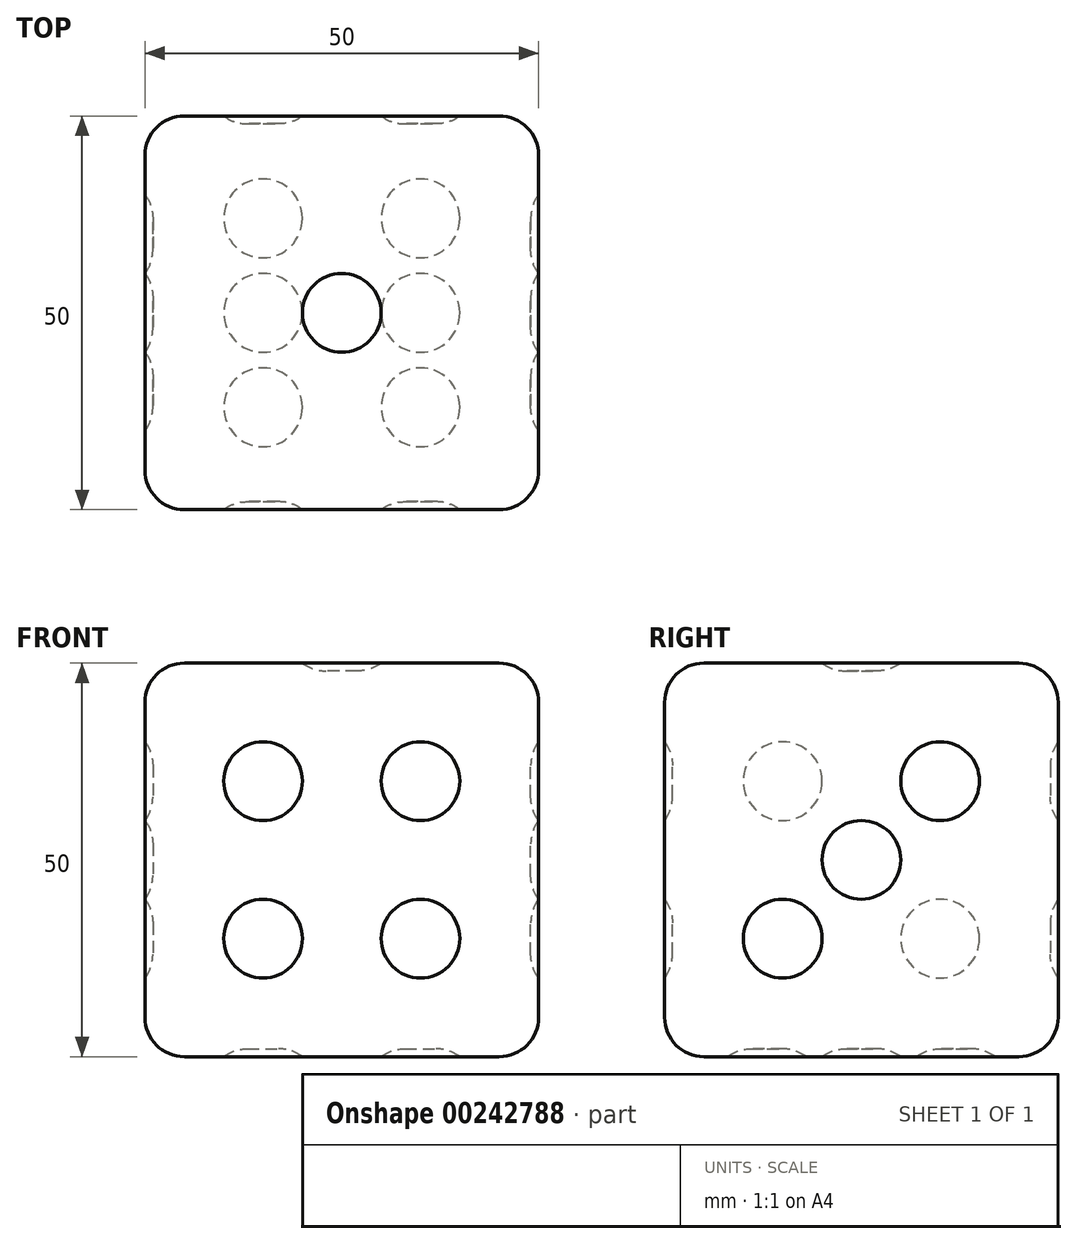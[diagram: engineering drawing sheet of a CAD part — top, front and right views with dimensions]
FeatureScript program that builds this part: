
annotation { "Feature Type Name" : "Feature", "Feature Type Description" : "" }
export const myFeature = defineFeature(function(context is Context, id is Id, definition is map)
    precondition{}
    {
        {
            var Q0;
            Q0=qCreatedBy(makeId("Top.planeOp"),FACE);
            var sketch = newSketch(context, id + "F0", { "sketchPlane" : qUnion([Q0])});
            skLineSegment(sketch, "E0", {"start": v(50, 0) * mm, "end": v(50, -50) * mm});
            skLineSegment(sketch, "E1", {"start": v(0, 0) * mm, "end": v(0, -50) * mm});
            skLineSegment(sketch, "E2", {"start": v(50, -50) * mm, "end": v(0, -50) * mm});
            skLineSegment(sketch, "E3", {"start": v(50, 0) * mm, "end": v(0, 0) * mm});
            skSolve(sketch);
        }
        {
            var Q0;
            Q0=makeQuery(id+"F0.imprint","IMPRINT",FACE,{"disambiguationData":[TD([[makeQuery(id+"F0.imprint","IMPRINT",EDGE,{"derivedFrom":sQuery(id+"F0.wireOp",EDGE,"E0")}),-1.0]])]});
            extrude(context, id + "F1", {"entities" : qUnion([Q0]), "depth" : 50 * mm});
        }
        {
            var Q0;
            Q0=makeQuery(id+"F1.opExtrude","CAP_FACE",FACE,{"disambiguationData":[OSD([sQuery(id+"F0.wireOp",EDGE,"E0"),sQuery(id+"F0.wireOp",EDGE,"E1"),sQuery(id+"F0.wireOp",EDGE,"E2"),sQuery(id+"F0.wireOp",EDGE,"E3")])],"isStart":false});
            var sketch = newSketch(context, id + "F2", { "sketchPlane" : qUnion([Q0])});
            skCircle(sketch, "E4", {"center": v(25, -25) * mm, "radius": 5 * mm});
            skSolve(sketch);
        }
        {
            var Q0;
            Q0=makeQuery(id+"F2.imprint","IMPRINT",FACE,{"disambiguationData":[TD([[makeQuery(id+"F2.imprint","IMPRINT",EDGE,{"derivedFrom":sQuery(id+"F2.wireOp",EDGE,"E4")}),1.0]])]});
            extrude(context, id + "F3", {"entities" : qUnion([Q0]), "operationType" : NewBodyOperationType.REMOVE, "oppositeDirection" : true, "depth" : 1 * mm});
        }
        {
            var Q0;
            Q0=makeQuery(id+"F1.opExtrude","SWEPT_EDGE",EDGE,{"disambiguationData":[OSD([sQuery(id+"F0.wireOp",EDGE,"E1"),sQuery(id+"F0.wireOp",EDGE,"E2")])]});
            var Q1;
            Q1=makeQuery(id+"F1.opExtrude","CAP_EDGE",EDGE,{"disambiguationData":[OSD([sQuery(id+"F0.wireOp",EDGE,"E2")])],"isStart":false});
            var Q2;
            Q2=makeQuery(id+"F1.opExtrude","CAP_EDGE",EDGE,{"disambiguationData":[OSD([sQuery(id+"F0.wireOp",EDGE,"E3")])],"isStart":false});
            var Q3;
            Q3=makeQuery(id+"F1.opExtrude","SWEPT_FACE",FACE,{"disambiguationData":[OSD([sQuery(id+"F0.wireOp",EDGE,"E1")])]});
            var Q4;
            Q4=makeQuery(id+"F1.opExtrude","CAP_EDGE",EDGE,{"disambiguationData":[OSD([sQuery(id+"F0.wireOp",EDGE,"E2")])],"isStart":true});
            var Q5;
            Q5=makeQuery(id+"F1.opExtrude","SWEPT_EDGE",EDGE,{"disambiguationData":[OSD([sQuery(id+"F0.wireOp",EDGE,"E0"),sQuery(id+"F0.wireOp",EDGE,"E2")])]});
            var Q6;
            Q6=makeQuery(id+"F1.opExtrude","CAP_EDGE",EDGE,{"disambiguationData":[OSD([sQuery(id+"F0.wireOp",EDGE,"E3")])],"isStart":true});
            var Q7;
            Q7=makeQuery(id+"F1.opExtrude","SWEPT_EDGE",EDGE,{"disambiguationData":[OSD([sQuery(id+"F0.wireOp",EDGE,"E0"),sQuery(id+"F0.wireOp",EDGE,"E3")])]});
            var Q8;
            Q8=makeQuery(id+"F1.opExtrude","CAP_EDGE",EDGE,{"disambiguationData":[OSD([sQuery(id+"F0.wireOp",EDGE,"E0")])],"isStart":true});
            var Q9;
            Q9=makeQuery(id+"F1.opExtrude","CAP_EDGE",EDGE,{"disambiguationData":[OSD([sQuery(id+"F0.wireOp",EDGE,"E0")])],"isStart":false});
            fillet(context, id + "F4", {"entities" : qUnion([Q0, Q1, Q2, Q3, Q4, Q5, Q6, Q7, Q8, Q9]), "radius" : 5 * mm, "tangentPropagation" : true, "allowEdgeOverflow" : false});
        }
        {
            var Q0;
            Q0=makeQuery(id+"F3.opExtrude","CAP_EDGE",EDGE,{"disambiguationData":[OSD([sQuery(id+"F2.wireOp",EDGE,"E4")])],"isStart":false});
            var Q1;
            Q1=makeQuery(id+"F3.boolean.opBoolean","COPY",EDGE,{"derivedFrom":makeQuery(id+"F3.opExtrude","CAP_EDGE",EDGE,{"disambiguationData":[OSD([sQuery(id+"F2.wireOp",EDGE,"E4")])],"isStart":false})});
            fillet(context, id + "F5", {"entities" : qUnion([Q0, Q1]), "radius" : 5 * mm, "tangentPropagation" : true, "allowEdgeOverflow" : false});
        }
        {
            var Q0;
            Q0=makeQuery(id+"F1.opExtrude","SWEPT_FACE",FACE,{"disambiguationData":[OSD([sQuery(id+"F0.wireOp",EDGE,"E2")])]});
            var sketch = newSketch(context, id + "F6", { "sketchPlane" : qUnion([Q0])});
            skCircle(sketch, "E5", {"center": v(35, 35) * mm, "radius": 5 * mm});
            skCircle(sketch, "E6", {"center": v(15, 15) * mm, "radius": 5 * mm});
            skCircle(sketch, "E7", {"center": v(15, 35) * mm, "radius": 5 * mm});
            skCircle(sketch, "E8", {"center": v(35, 15) * mm, "radius": 5 * mm});
            skSolve(sketch);
        }
        {
            var Q0;
            Q0=makeQuery(id+"F6.imprint","IMPRINT",FACE,{"disambiguationData":[TD([[makeQuery(id+"F6.imprint","IMPRINT",EDGE,{"derivedFrom":sQuery(id+"F6.wireOp",EDGE,"E7")}),1.0]])]});
            var Q1;
            Q1=makeQuery(id+"F6.imprint","IMPRINT",FACE,{"disambiguationData":[TD([[makeQuery(id+"F6.imprint","IMPRINT",EDGE,{"derivedFrom":sQuery(id+"F6.wireOp",EDGE,"E5")}),1.0]])]});
            var Q2;
            Q2=makeQuery(id+"F6.imprint","IMPRINT",FACE,{"disambiguationData":[TD([[makeQuery(id+"F6.imprint","IMPRINT",EDGE,{"derivedFrom":sQuery(id+"F6.wireOp",EDGE,"E8")}),1.0]])]});
            var Q3;
            Q3=makeQuery(id+"F6.imprint","IMPRINT",FACE,{"disambiguationData":[TD([[makeQuery(id+"F6.imprint","IMPRINT",EDGE,{"derivedFrom":sQuery(id+"F6.wireOp",EDGE,"E6")}),1.0]])]});
            extrude(context, id + "F7", {"entities" : qUnion([Q0, Q1, Q2, Q3]), "operationType" : NewBodyOperationType.REMOVE, "oppositeDirection" : true, "depth" : 1 * mm});
        }
        {
            var Q0;
            Q0=makeQuery(id+"F7.opExtrude","CAP_EDGE",EDGE,{"disambiguationData":[OSD([sQuery(id+"F6.wireOp",EDGE,"E7")])],"isStart":false});
            var Q1;
            Q1=makeQuery(id+"F7.opExtrude","CAP_EDGE",EDGE,{"disambiguationData":[OSD([sQuery(id+"F6.wireOp",EDGE,"E5")])],"isStart":false});
            var Q2;
            Q2=makeQuery(id+"F7.opExtrude","CAP_EDGE",EDGE,{"disambiguationData":[OSD([sQuery(id+"F6.wireOp",EDGE,"E6")])],"isStart":false});
            var Q3;
            Q3=makeQuery(id+"F7.opExtrude","CAP_EDGE",EDGE,{"disambiguationData":[OSD([sQuery(id+"F6.wireOp",EDGE,"E8")])],"isStart":false});
            var Q4;
            Q4=makeQuery(id+"F7.boolean.opBoolean","COPY",EDGE,{"derivedFrom":makeQuery(id+"F7.opExtrude","CAP_EDGE",EDGE,{"disambiguationData":[OSD([sQuery(id+"F6.wireOp",EDGE,"E7")])],"isStart":false})});
            var Q5;
            Q5=makeQuery(id+"F7.boolean.opBoolean","COPY",EDGE,{"derivedFrom":makeQuery(id+"F7.opExtrude","CAP_EDGE",EDGE,{"disambiguationData":[OSD([sQuery(id+"F6.wireOp",EDGE,"E5")])],"isStart":false})});
            var Q6;
            Q6=makeQuery(id+"F7.boolean.opBoolean","COPY",EDGE,{"derivedFrom":makeQuery(id+"F7.opExtrude","CAP_EDGE",EDGE,{"disambiguationData":[OSD([sQuery(id+"F6.wireOp",EDGE,"E8")])],"isStart":false})});
            var Q7;
            Q7=makeQuery(id+"F7.boolean.opBoolean","COPY",EDGE,{"derivedFrom":makeQuery(id+"F7.opExtrude","CAP_EDGE",EDGE,{"disambiguationData":[OSD([sQuery(id+"F6.wireOp",EDGE,"E6")])],"isStart":false})});
            fillet(context, id + "F8", {"entities" : qUnion([Q0, Q1, Q2, Q3, Q4, Q5, Q6, Q7]), "radius" : 5 * mm, "tangentPropagation" : true, "allowEdgeOverflow" : false});
        }
        {
            var Q0;
            Q0=makeQuery(id+"F1.opExtrude","SWEPT_FACE",FACE,{"disambiguationData":[OSD([sQuery(id+"F0.wireOp",EDGE,"E3")])]});
            var sketch = newSketch(context, id + "F9", { "sketchPlane" : qUnion([Q0])});
            skCircle(sketch, "E9", {"center": v(-15, 35) * mm, "radius": 5 * mm});
            skCircle(sketch, "E10", {"center": v(-35, 15) * mm, "radius": 5 * mm});
            skSolve(sketch);
        }
        {
            var Q0;
            Q0=makeQuery(id+"F9.imprint","IMPRINT",FACE,{"disambiguationData":[TD([[makeQuery(id+"F9.imprint","IMPRINT",EDGE,{"derivedFrom":sQuery(id+"F9.wireOp",EDGE,"E10")}),1.0]])]});
            var Q1;
            Q1=makeQuery(id+"F9.imprint","IMPRINT",FACE,{"disambiguationData":[TD([[makeQuery(id+"F9.imprint","IMPRINT",EDGE,{"derivedFrom":sQuery(id+"F9.wireOp",EDGE,"E9")}),1.0]])]});
            extrude(context, id + "F10", {"entities" : qUnion([Q0, Q1]), "operationType" : NewBodyOperationType.REMOVE, "oppositeDirection" : true, "depth" : 1 * mm});
        }
        {
            var Q0;
            Q0=makeQuery(id+"F10.opExtrude","CAP_EDGE",EDGE,{"disambiguationData":[OSD([sQuery(id+"F9.wireOp",EDGE,"E10")])],"isStart":false});
            var Q1;
            Q1=makeQuery(id+"F10.opExtrude","CAP_EDGE",EDGE,{"disambiguationData":[OSD([sQuery(id+"F9.wireOp",EDGE,"E9")])],"isStart":false});
            var Q2;
            Q2=makeQuery(id+"F10.boolean.opBoolean","COPY",EDGE,{"derivedFrom":makeQuery(id+"F10.opExtrude","CAP_EDGE",EDGE,{"disambiguationData":[OSD([sQuery(id+"F9.wireOp",EDGE,"E9")])],"isStart":false})});
            var Q3;
            Q3=makeQuery(id+"F10.boolean.opBoolean","COPY",EDGE,{"derivedFrom":makeQuery(id+"F10.opExtrude","CAP_EDGE",EDGE,{"disambiguationData":[OSD([sQuery(id+"F9.wireOp",EDGE,"E10")])],"isStart":false})});
            fillet(context, id + "F11", {"entities" : qUnion([Q0, Q1, Q2, Q3]), "radius" : 5 * mm, "tangentPropagation" : true, "allowEdgeOverflow" : false});
        }
        {
            var Q0;
            Q0=makeQuery(id+"F1.opExtrude","SWEPT_FACE",FACE,{"disambiguationData":[OSD([sQuery(id+"F0.wireOp",EDGE,"E0")])]});
            var sketch = newSketch(context, id + "F12", { "sketchPlane" : qUnion([Q0])});
            skCircle(sketch, "E11", {"center": v(-35, 15) * mm, "radius": 5 * mm});
            skCircle(sketch, "E12", {"center": v(-25, 25) * mm, "radius": 5 * mm});
            skCircle(sketch, "E13", {"center": v(-15, 35) * mm, "radius": 5 * mm});
            skSolve(sketch);
        }
        {
            var Q0;
            Q0=makeQuery(id+"F12.imprint","IMPRINT",FACE,{"disambiguationData":[TD([[makeQuery(id+"F12.imprint","IMPRINT",EDGE,{"derivedFrom":sQuery(id+"F12.wireOp",EDGE,"E13")}),1.0]])]});
            var Q1;
            Q1=makeQuery(id+"F12.imprint","IMPRINT",FACE,{"disambiguationData":[TD([[makeQuery(id+"F12.imprint","IMPRINT",EDGE,{"derivedFrom":sQuery(id+"F12.wireOp",EDGE,"E12")}),1.0]])]});
            var Q2;
            Q2=makeQuery(id+"F12.imprint","IMPRINT",FACE,{"disambiguationData":[TD([[makeQuery(id+"F12.imprint","IMPRINT",EDGE,{"derivedFrom":sQuery(id+"F12.wireOp",EDGE,"E11")}),1.0]])]});
            extrude(context, id + "F13", {"entities" : qUnion([Q0, Q1, Q2]), "operationType" : NewBodyOperationType.REMOVE, "oppositeDirection" : true, "depth" : 1 * mm});
        }
        {
            var Q0;
            Q0=makeQuery(id+"F13.opExtrude","CAP_EDGE",EDGE,{"disambiguationData":[OSD([sQuery(id+"F12.wireOp",EDGE,"E11")])],"isStart":false});
            var Q1;
            Q1=makeQuery(id+"F13.opExtrude","CAP_EDGE",EDGE,{"disambiguationData":[OSD([sQuery(id+"F12.wireOp",EDGE,"E12")])],"isStart":false});
            var Q2;
            Q2=makeQuery(id+"F13.opExtrude","CAP_EDGE",EDGE,{"disambiguationData":[OSD([sQuery(id+"F12.wireOp",EDGE,"E13")])],"isStart":false});
            var Q3;
            Q3=makeQuery(id+"F13.boolean.opBoolean","COPY",EDGE,{"derivedFrom":makeQuery(id+"F13.opExtrude","CAP_EDGE",EDGE,{"disambiguationData":[OSD([sQuery(id+"F12.wireOp",EDGE,"E11")])],"isStart":false})});
            var Q4;
            Q4=makeQuery(id+"F13.boolean.opBoolean","COPY",EDGE,{"derivedFrom":makeQuery(id+"F13.opExtrude","CAP_EDGE",EDGE,{"disambiguationData":[OSD([sQuery(id+"F12.wireOp",EDGE,"E13")])],"isStart":false})});
            var Q5;
            Q5=makeQuery(id+"F13.boolean.opBoolean","COPY",EDGE,{"derivedFrom":makeQuery(id+"F13.opExtrude","CAP_EDGE",EDGE,{"disambiguationData":[OSD([sQuery(id+"F12.wireOp",EDGE,"E12")])],"isStart":false})});
            fillet(context, id + "F14", {"entities" : qUnion([Q0, Q1, Q2, Q3, Q4, Q5]), "radius" : 5 * mm, "tangentPropagation" : true, "allowEdgeOverflow" : false});
        }
        {
            var Q0;
            Q0=makeQuery(id+"F1.opExtrude","SWEPT_FACE",FACE,{"disambiguationData":[OSD([sQuery(id+"F0.wireOp",EDGE,"E1")])]});
            var sketch = newSketch(context, id + "F15", { "sketchPlane" : qUnion([Q0])});
            skCircle(sketch, "E14", {"center": v(25, 25) * mm, "radius": 5 * mm});
            skCircle(sketch, "E15", {"center": v(15, 15) * mm, "radius": 5 * mm});
            skCircle(sketch, "E16", {"center": v(35, 15) * mm, "radius": 5 * mm});
            skCircle(sketch, "E17", {"center": v(15, 35) * mm, "radius": 5 * mm});
            skCircle(sketch, "E18", {"center": v(35, 35) * mm, "radius": 5 * mm});
            skSolve(sketch);
        }
        {
            var Q0;
            Q0=makeQuery(id+"F15.imprint","IMPRINT",FACE,{"disambiguationData":[TD([[makeQuery(id+"F15.imprint","IMPRINT",EDGE,{"derivedFrom":sQuery(id+"F15.wireOp",EDGE,"E17")}),1.0]])]});
            var Q1;
            Q1=makeQuery(id+"F15.imprint","IMPRINT",FACE,{"disambiguationData":[TD([[makeQuery(id+"F15.imprint","IMPRINT",EDGE,{"derivedFrom":sQuery(id+"F15.wireOp",EDGE,"E14")}),1.0]])]});
            var Q2;
            Q2=makeQuery(id+"F15.imprint","IMPRINT",FACE,{"disambiguationData":[TD([[makeQuery(id+"F15.imprint","IMPRINT",EDGE,{"derivedFrom":sQuery(id+"F15.wireOp",EDGE,"E15")}),1.0]])]});
            var Q3;
            Q3=makeQuery(id+"F15.imprint","IMPRINT",FACE,{"disambiguationData":[TD([[makeQuery(id+"F15.imprint","IMPRINT",EDGE,{"derivedFrom":sQuery(id+"F15.wireOp",EDGE,"E16")}),1.0]])]});
            var Q4;
            Q4=makeQuery(id+"F15.imprint","IMPRINT",FACE,{"disambiguationData":[TD([[makeQuery(id+"F15.imprint","IMPRINT",EDGE,{"derivedFrom":sQuery(id+"F15.wireOp",EDGE,"E18")}),1.0]])]});
            extrude(context, id + "F16", {"entities" : qUnion([Q0, Q1, Q2, Q3, Q4]), "operationType" : NewBodyOperationType.REMOVE, "oppositeDirection" : true, "depth" : 1 * mm});
        }
        {
            var Q0;
            Q0=makeQuery(id+"F16.opExtrude","CAP_EDGE",EDGE,{"disambiguationData":[OSD([sQuery(id+"F15.wireOp",EDGE,"E17")])],"isStart":false});
            var Q1;
            Q1=makeQuery(id+"F16.opExtrude","CAP_EDGE",EDGE,{"disambiguationData":[OSD([sQuery(id+"F15.wireOp",EDGE,"E14")])],"isStart":false});
            var Q2;
            Q2=makeQuery(id+"F16.opExtrude","CAP_EDGE",EDGE,{"disambiguationData":[OSD([sQuery(id+"F15.wireOp",EDGE,"E16")])],"isStart":false});
            var Q3;
            Q3=makeQuery(id+"F16.opExtrude","CAP_EDGE",EDGE,{"disambiguationData":[OSD([sQuery(id+"F15.wireOp",EDGE,"E18")])],"isStart":false});
            var Q4;
            Q4=makeQuery(id+"F16.opExtrude","CAP_EDGE",EDGE,{"disambiguationData":[OSD([sQuery(id+"F15.wireOp",EDGE,"E15")])],"isStart":false});
            var Q5;
            Q5=makeQuery(id+"F16.boolean.opBoolean","COPY",EDGE,{"derivedFrom":makeQuery(id+"F16.opExtrude","CAP_EDGE",EDGE,{"disambiguationData":[OSD([sQuery(id+"F15.wireOp",EDGE,"E16")])],"isStart":false})});
            var Q6;
            Q6=makeQuery(id+"F16.boolean.opBoolean","COPY",EDGE,{"derivedFrom":makeQuery(id+"F16.opExtrude","CAP_EDGE",EDGE,{"disambiguationData":[OSD([sQuery(id+"F15.wireOp",EDGE,"E15")])],"isStart":false})});
            var Q7;
            Q7=makeQuery(id+"F16.boolean.opBoolean","COPY",EDGE,{"derivedFrom":makeQuery(id+"F16.opExtrude","CAP_EDGE",EDGE,{"disambiguationData":[OSD([sQuery(id+"F15.wireOp",EDGE,"E14")])],"isStart":false})});
            var Q8;
            Q8=makeQuery(id+"F16.boolean.opBoolean","COPY",EDGE,{"derivedFrom":makeQuery(id+"F16.opExtrude","CAP_EDGE",EDGE,{"disambiguationData":[OSD([sQuery(id+"F15.wireOp",EDGE,"E18")])],"isStart":false})});
            var Q9;
            Q9=makeQuery(id+"F16.boolean.opBoolean","COPY",EDGE,{"derivedFrom":makeQuery(id+"F16.opExtrude","CAP_EDGE",EDGE,{"disambiguationData":[OSD([sQuery(id+"F15.wireOp",EDGE,"E17")])],"isStart":false})});
            fillet(context, id + "F17", {"entities" : qUnion([Q0, Q1, Q2, Q3, Q4, Q5, Q6, Q7, Q8, Q9]), "radius" : 5 * mm, "tangentPropagation" : true, "allowEdgeOverflow" : false});
        }
        {
            var Q0;
            Q0=makeQuery(id+"F1.opExtrude","CAP_FACE",FACE,{"disambiguationData":[OSD([sQuery(id+"F0.wireOp",EDGE,"E0"),sQuery(id+"F0.wireOp",EDGE,"E1"),sQuery(id+"F0.wireOp",EDGE,"E2"),sQuery(id+"F0.wireOp",EDGE,"E3")])],"isStart":true});
            var sketch = newSketch(context, id + "F18", { "sketchPlane" : qUnion([Q0])});
            skCircle(sketch, "E19", {"center": v(15, 25) * mm, "radius": 5 * mm});
            skCircle(sketch, "E20", {"center": v(35, 25) * mm, "radius": 5 * mm});
            skCircle(sketch, "E21", {"center": v(15, 37) * mm, "radius": 5 * mm});
            skCircle(sketch, "E22", {"center": v(35, 37) * mm, "radius": 5 * mm});
            skCircle(sketch, "E23", {"center": v(35, 13) * mm, "radius": 5 * mm});
            skCircle(sketch, "E24", {"center": v(15, 13) * mm, "radius": 5 * mm});
            skSolve(sketch);
        }
        {
            var Q0;
            Q0=makeQuery(id+"F18.imprint","IMPRINT",FACE,{"disambiguationData":[TD([[makeQuery(id+"F18.imprint","IMPRINT",EDGE,{"derivedFrom":sQuery(id+"F18.wireOp",EDGE,"E21")}),1.0]])]});
            var Q1;
            Q1=makeQuery(id+"F18.imprint","IMPRINT",FACE,{"disambiguationData":[TD([[makeQuery(id+"F18.imprint","IMPRINT",EDGE,{"derivedFrom":sQuery(id+"F18.wireOp",EDGE,"E19")}),1.0]])]});
            var Q2;
            Q2=makeQuery(id+"F18.imprint","IMPRINT",FACE,{"disambiguationData":[TD([[makeQuery(id+"F18.imprint","IMPRINT",EDGE,{"derivedFrom":sQuery(id+"F18.wireOp",EDGE,"E24")}),1.0]])]});
            var Q3;
            Q3=makeQuery(id+"F18.imprint","IMPRINT",FACE,{"disambiguationData":[TD([[makeQuery(id+"F18.imprint","IMPRINT",EDGE,{"derivedFrom":sQuery(id+"F18.wireOp",EDGE,"E22")}),1.0]])]});
            var Q4;
            Q4=makeQuery(id+"F18.imprint","IMPRINT",FACE,{"disambiguationData":[TD([[makeQuery(id+"F18.imprint","IMPRINT",EDGE,{"derivedFrom":sQuery(id+"F18.wireOp",EDGE,"E23")}),1.0]])]});
            var Q5;
            Q5=makeQuery(id+"F18.imprint","IMPRINT",FACE,{"disambiguationData":[TD([[makeQuery(id+"F18.imprint","IMPRINT",EDGE,{"derivedFrom":sQuery(id+"F18.wireOp",EDGE,"E20")}),1.0]])]});
            extrude(context, id + "F19", {"entities" : qUnion([Q0, Q1, Q2, Q3, Q4, Q5]), "operationType" : NewBodyOperationType.REMOVE, "oppositeDirection" : true, "depth" : 1 * mm});
        }
        {
            var Q0;
            Q0=makeQuery(id+"F19.opExtrude","CAP_EDGE",EDGE,{"disambiguationData":[OSD([sQuery(id+"F18.wireOp",EDGE,"5FOLEQR7-44Id-jB8M-p0gz-kIlaQh1qTy6j")])],"isStart":false});
            var Q1;
            Q1=makeQuery(id+"F19.opExtrude","CAP_EDGE",EDGE,{"disambiguationData":[OSD([sQuery(id+"F18.wireOp",EDGE,"lmUNnAq0-RdFQ-vipd-3jg9-gK4JFa1s3IPS")])],"isStart":false});
            var Q2;
            Q2=makeQuery(id+"F19.opExtrude","CAP_EDGE",EDGE,{"disambiguationData":[OSD([sQuery(id+"F18.wireOp",EDGE,"E20")])],"isStart":false});
            var Q3;
            Q3=makeQuery(id+"F19.opExtrude","CAP_EDGE",EDGE,{"disambiguationData":[OSD([sQuery(id+"F18.wireOp",EDGE,"E19")])],"isStart":false});
            var Q4;
            Q4=makeQuery(id+"F19.opExtrude","CAP_EDGE",EDGE,{"disambiguationData":[OSD([sQuery(id+"F18.wireOp",EDGE,"V0HSiJgt-mlXV-lJPM-J4ov-odtx1VyCKhui")])],"isStart":false});
            var Q5;
            Q5=makeQuery(id+"F19.opExtrude","CAP_EDGE",EDGE,{"disambiguationData":[OSD([sQuery(id+"F18.wireOp",EDGE,"KUiKgVB0-WbgK-Yf4m-yarB-RqFe6iAfvPle")])],"isStart":false});
            var Q6;
            Q6=makeQuery(id+"F19.opExtrude","CAP_EDGE",EDGE,{"disambiguationData":[OSD([sQuery(id+"F18.wireOp",EDGE,"E21")])],"isStart":false});
            var Q7;
            Q7=makeQuery(id+"F19.opExtrude","CAP_EDGE",EDGE,{"disambiguationData":[OSD([sQuery(id+"F18.wireOp",EDGE,"E24")])],"isStart":false});
            var Q8;
            Q8=makeQuery(id+"F19.opExtrude","CAP_EDGE",EDGE,{"disambiguationData":[OSD([sQuery(id+"F18.wireOp",EDGE,"E23")])],"isStart":false});
            var Q9;
            Q9=makeQuery(id+"F19.opExtrude","CAP_EDGE",EDGE,{"disambiguationData":[OSD([sQuery(id+"F18.wireOp",EDGE,"E22")])],"isStart":false});
            var Q10;
            Q10=makeQuery(id+"F19.boolean.opBoolean","COPY",EDGE,{"derivedFrom":makeQuery(id+"F19.opExtrude","CAP_EDGE",EDGE,{"disambiguationData":[OSD([sQuery(id+"F18.wireOp",EDGE,"E22")])],"isStart":false})});
            var Q11;
            Q11=makeQuery(id+"F19.boolean.opBoolean","COPY",EDGE,{"derivedFrom":makeQuery(id+"F19.opExtrude","CAP_EDGE",EDGE,{"disambiguationData":[OSD([sQuery(id+"F18.wireOp",EDGE,"E21")])],"isStart":false})});
            var Q12;
            Q12=makeQuery(id+"F19.boolean.opBoolean","COPY",EDGE,{"derivedFrom":makeQuery(id+"F19.opExtrude","CAP_EDGE",EDGE,{"disambiguationData":[OSD([sQuery(id+"F18.wireOp",EDGE,"E19")])],"isStart":false})});
            var Q13;
            Q13=makeQuery(id+"F19.boolean.opBoolean","COPY",EDGE,{"derivedFrom":makeQuery(id+"F19.opExtrude","CAP_EDGE",EDGE,{"disambiguationData":[OSD([sQuery(id+"F18.wireOp",EDGE,"E24")])],"isStart":false})});
            var Q14;
            Q14=makeQuery(id+"F19.boolean.opBoolean","COPY",EDGE,{"derivedFrom":makeQuery(id+"F19.opExtrude","CAP_EDGE",EDGE,{"disambiguationData":[OSD([sQuery(id+"F18.wireOp",EDGE,"E20")])],"isStart":false})});
            var Q15;
            Q15=makeQuery(id+"F19.boolean.opBoolean","COPY",EDGE,{"derivedFrom":makeQuery(id+"F19.opExtrude","CAP_EDGE",EDGE,{"disambiguationData":[OSD([sQuery(id+"F18.wireOp",EDGE,"E23")])],"isStart":false})});
            fillet(context, id + "F20", {"entities" : qUnion([Q0, Q1, Q2, Q3, Q4, Q5, Q6, Q7, Q8, Q9, Q10, Q11, Q12, Q13, Q14, Q15]), "radius" : 5 * mm, "tangentPropagation" : true, "allowEdgeOverflow" : false});
        }
        {
            var Q0;
            Q0=makeQuery(id+"F1.opExtrude","CAP_FACE",FACE,{"disambiguationData":[OSD([sQuery(id+"F0.wireOp",EDGE,"E0"),sQuery(id+"F0.wireOp",EDGE,"E1"),sQuery(id+"F0.wireOp",EDGE,"E2"),sQuery(id+"F0.wireOp",EDGE,"E3")])],"isStart":true});
            extrude(context, id + "F21", {"entities" : qUnion([Q0]), "operationType" : NewBodyOperationType.ADD, "oppositeDirection" : true, "depth" : 0.5 * mm});
        }
    });
